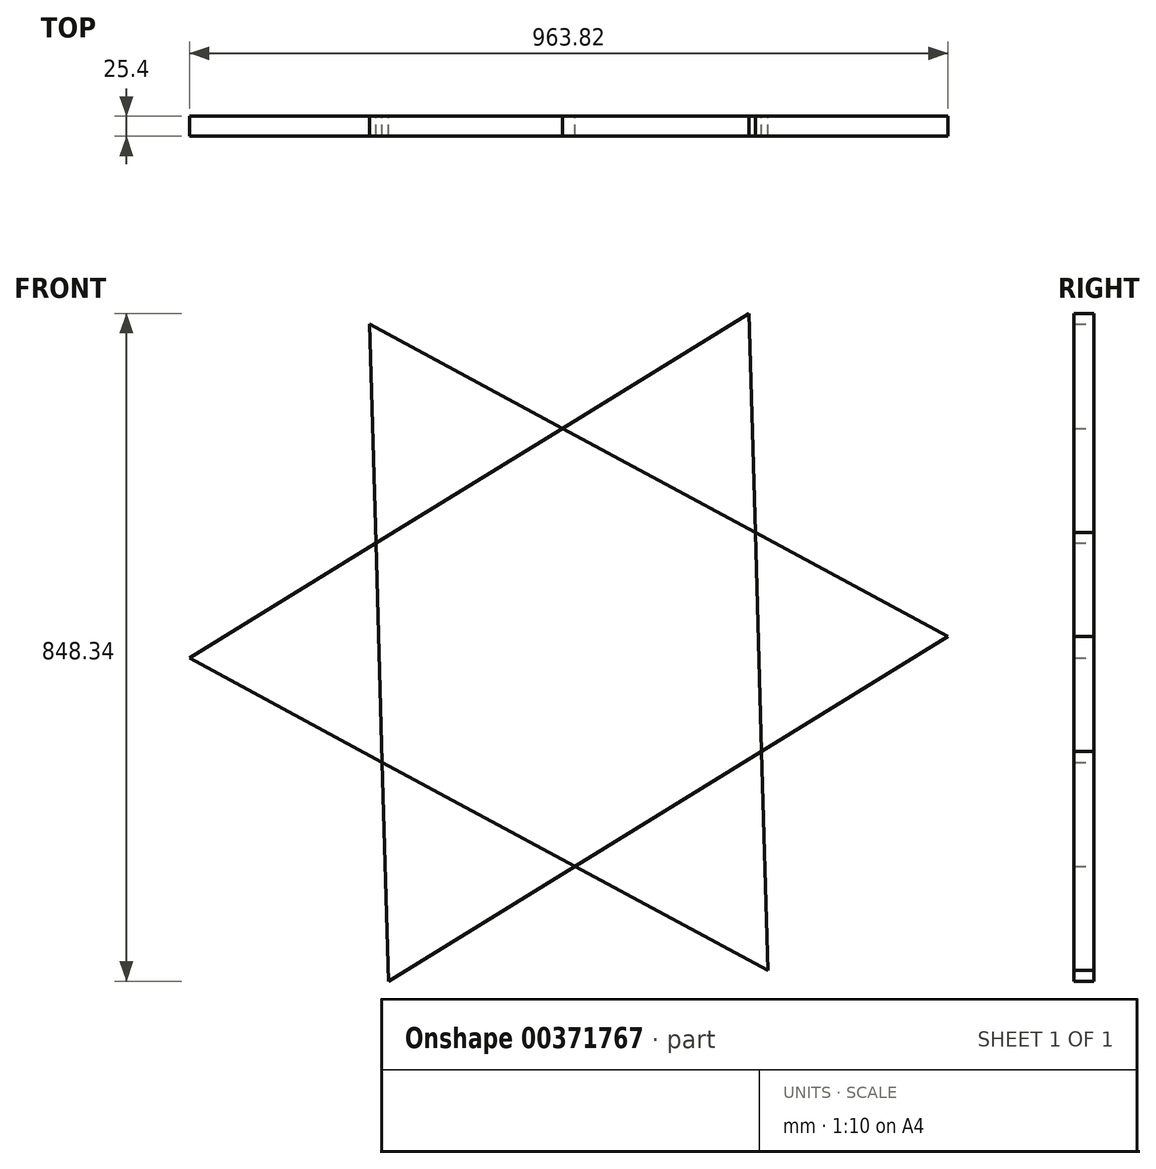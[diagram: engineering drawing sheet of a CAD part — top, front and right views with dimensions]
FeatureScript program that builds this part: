
annotation { "Feature Type Name" : "Feature", "Feature Type Description" : "" }
export const myFeature = defineFeature(function(context is Context, id is Id, definition is map)
    precondition{}
    {
        {
            var Q0;
            Q0=qCreatedBy(makeId("Front.planeOp"),FACE);
            var sketch = newSketch(context, id + "F0", { "sketchPlane" : qUnion([Q0])});
            skCircle(sketch, "E0.cCircle", {"center": v(0, 0) * mm, "radius": 417.51 * mm, "construction": true});
            skLineSegment(sketch, "E0.0", {"start": v(481.9, 13.65) * mm, "end": v(252.78, -410.52) * mm});
            skLineSegment(sketch, "E0.1", {"start": v(252.78, -410.52) * mm, "end": v(-229.13, -424.17) * mm});
            skLineSegment(sketch, "E0.2", {"start": v(-229.13, -424.17) * mm, "end": v(-481.9, -13.65) * mm});
            skLineSegment(sketch, "E0.3", {"start": v(-481.9, -13.65) * mm, "end": v(-252.78, 410.52) * mm});
            skLineSegment(sketch, "E0.4", {"start": v(-252.78, 410.52) * mm, "end": v(229.13, 424.17) * mm});
            skLineSegment(sketch, "E0.5", {"start": v(229.13, 424.17) * mm, "end": v(481.9, 13.65) * mm});
            skPoint(sketch, "E0.0.midPoint", {"position": v(367.34, -198.44) * mm});
            skLineSegment(sketch, "E1", {"start": v(-252.78, 410.52) * mm, "end": v(481.9, 13.65) * mm});
            skLineSegment(sketch, "E2", {"start": v(481.9, 13.65) * mm, "end": v(-229.13, -424.17) * mm});
            skLineSegment(sketch, "E3", {"start": v(-252.78, 410.52) * mm, "end": v(-229.13, -424.17) * mm});
            skLineSegment(sketch, "E4", {"start": v(-481.9, -13.65) * mm, "end": v(252.78, -410.52) * mm});
            skLineSegment(sketch, "E5", {"start": v(252.78, -410.52) * mm, "end": v(229.13, 424.17) * mm});
            skLineSegment(sketch, "E6", {"start": v(229.13, 424.17) * mm, "end": v(-481.9, -13.65) * mm});
            skSolve(sketch);
        }
        {
            var Q0;
            {var subQ0=sQuery(id+"F0.wireOp",EDGE,"E6");var subQ1=sQuery(id+"F0.wireOp",EDGE,"E3");var subQ2=makeQuery(id+"F0.imprint","INTERSECT",VERTEX,{"derivedFrom":[subQ1,subQ0]});Q0=makeQuery(id+"F0.imprint","IMPRINT",FACE,{"disambiguationData":[TD([[makeQuery(id+"F0.imprint","IMPRINT",EDGE,{"disambiguationData":[TD([[subQ2,-1.0]])],"derivedFrom":subQ1}),-1.0]])]});}
            var Q1;
            {var subQ1=sQuery(id+"F0.wireOp",EDGE,"E2");var subQ3=sQuery(id+"F0.wireOp",EDGE,"E4");var subQ4=makeQuery(id+"F0.imprint","INTERSECT",VERTEX,{"derivedFrom":[subQ1,subQ3]});Q1=makeQuery(id+"F0.imprint","IMPRINT",FACE,{"disambiguationData":[TD([[makeQuery(id+"F0.imprint","IMPRINT",EDGE,{"disambiguationData":[TD([[subQ4,1.0]])],"derivedFrom":subQ3}),-1.0]])]});}
            var Q2;
            {var subQ0=sQuery(id+"F0.wireOp",EDGE,"E5");var subQ1=sQuery(id+"F0.wireOp",EDGE,"E2");var subQ2=makeQuery(id+"F0.imprint","INTERSECT",VERTEX,{"derivedFrom":[subQ1,subQ0]});Q2=makeQuery(id+"F0.imprint","IMPRINT",FACE,{"disambiguationData":[TD([[makeQuery(id+"F0.imprint","IMPRINT",EDGE,{"disambiguationData":[TD([[subQ2,-1.0]])],"derivedFrom":subQ1}),1.0]])]});}
            var Q3;
            {var subQ1=sQuery(id+"F0.wireOp",EDGE,"E1");var subQ3=sQuery(id+"F0.wireOp",EDGE,"E5");var subQ4=makeQuery(id+"F0.imprint","INTERSECT",VERTEX,{"derivedFrom":[subQ1,subQ3]});Q3=makeQuery(id+"F0.imprint","IMPRINT",FACE,{"disambiguationData":[TD([[makeQuery(id+"F0.imprint","IMPRINT",EDGE,{"disambiguationData":[TD([[subQ4,1.0]])],"derivedFrom":subQ3}),-1.0]])]});}
            var Q4;
            {var subQ0=sQuery(id+"F0.wireOp",EDGE,"E6");var subQ1=sQuery(id+"F0.wireOp",EDGE,"E1");var subQ2=makeQuery(id+"F0.imprint","INTERSECT",VERTEX,{"derivedFrom":[subQ1,subQ0]});Q4=makeQuery(id+"F0.imprint","IMPRINT",FACE,{"disambiguationData":[TD([[makeQuery(id+"F0.imprint","IMPRINT",EDGE,{"disambiguationData":[TD([[subQ2,-1.0]])],"derivedFrom":subQ1}),1.0]])]});}
            var Q5;
            {var subQ1=sQuery(id+"F0.wireOp",EDGE,"E1");var subQ3=sQuery(id+"F0.wireOp",EDGE,"E6");var subQ4=makeQuery(id+"F0.imprint","INTERSECT",VERTEX,{"derivedFrom":[subQ1,subQ3]});Q5=makeQuery(id+"F0.imprint","IMPRINT",FACE,{"disambiguationData":[TD([[makeQuery(id+"F0.imprint","IMPRINT",EDGE,{"disambiguationData":[TD([[subQ4,-1.0]])],"derivedFrom":subQ3}),-1.0]])]});}
            extrude(context, id + "F1", {"entities" : qUnion([Q0, Q1, Q2, Q3, Q4, Q5]), "depth" : 25.4 * mm});
        }
    });
